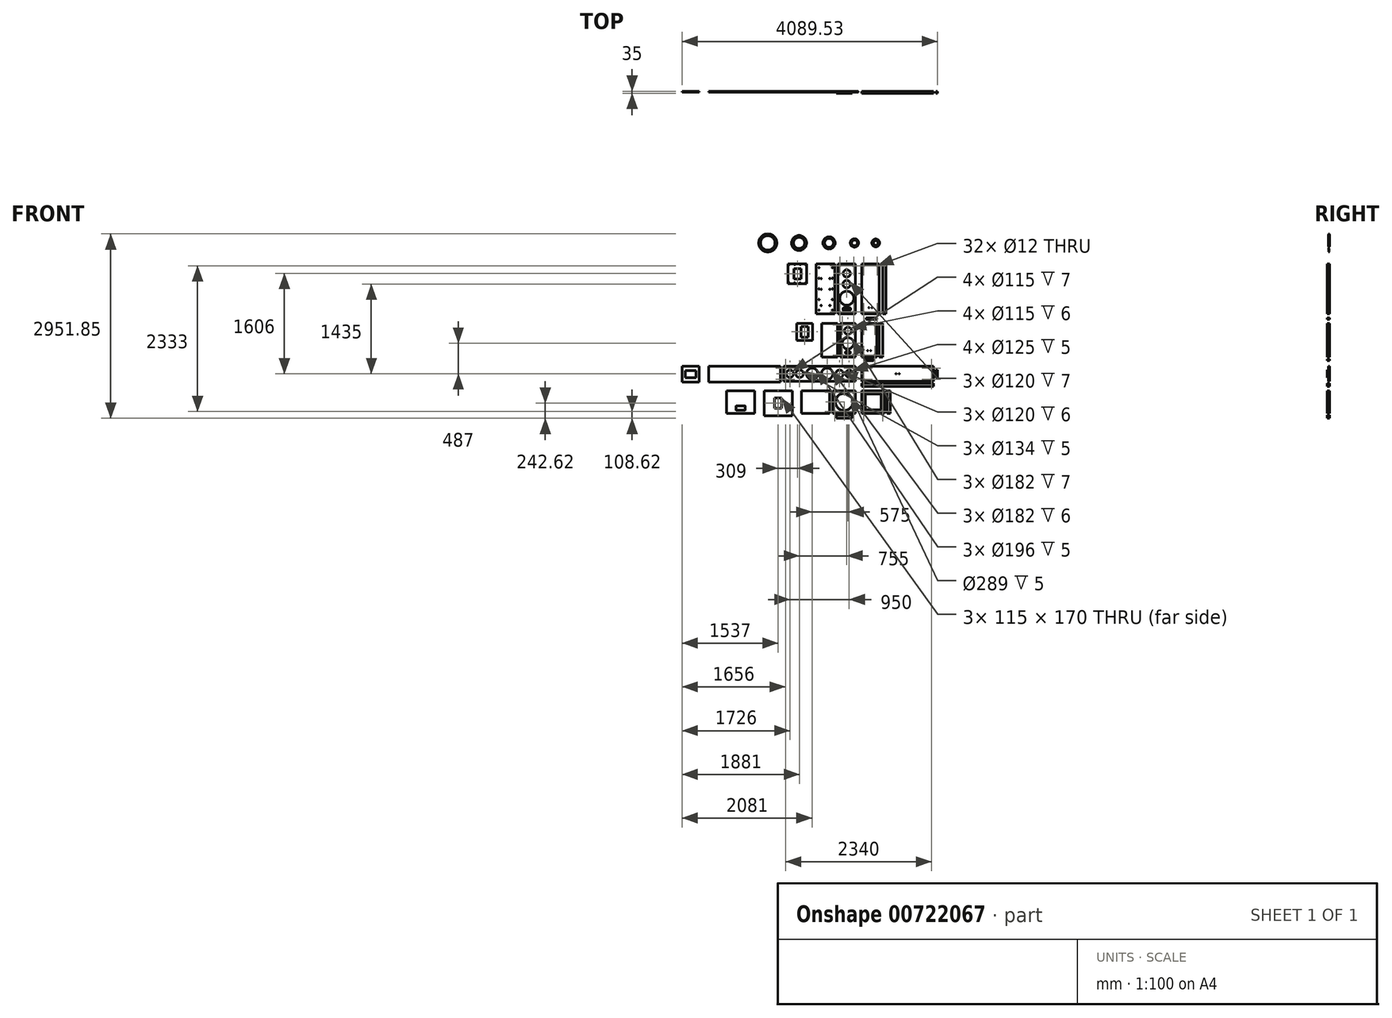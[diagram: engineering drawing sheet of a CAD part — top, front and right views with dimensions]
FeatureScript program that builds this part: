
annotation { "Feature Type Name" : "Feature", "Feature Type Description" : "" }
export const myFeature = defineFeature(function(context is Context, id is Id, definition is map)
    precondition{}
    {
        {
            assignVariable(context, id + "F0", {"name" : "WoodW", "anyValue" : 18});
        }
        {
            var Q0;
            Q0=qCreatedBy(makeId("Front.planeOp"),FACE);
            var sketch = newSketch(context, id + "F1", { "sketchPlane" : qUnion([Q0])});
            skLineSegment(sketch, "E0.bottom", {"start": v(0, 400) * mm, "end": v(-280, 400) * mm});
            skLineSegment(sketch, "E0.top", {"start": v(0, -400) * mm, "end": v(-280, -400) * mm});
            skLineSegment(sketch, "E0.left", {"start": v(0, 400) * mm, "end": v(0, -400) * mm});
            skLineSegment(sketch, "E0.right", {"start": v(-280, 400) * mm, "end": v(-280, -400) * mm});
            skLineSegment(sketch, "E1", {"start": v(-140, 400) * mm, "end": v(-140, -400) * mm, "construction": true});
            skCircle(sketch, "E2", {"center": v(-250, 370) * mm, "radius": 6 * mm});
            skCircle(sketch, "E3.MirrorC", {"center": v(-30, 370) * mm, "radius": 6 * mm});
            skCircle(sketch, "E4.MirrorC", {"center": v(-30, -370) * mm, "radius": 6 * mm});
            skCircle(sketch, "E5.MirrorC", {"center": v(-250, -370) * mm, "radius": 6 * mm});
            skLineSegment(sketch, "E6", {"start": v(50, -72.62) * mm, "end": v(50, -2297.12) * mm, "construction": true});
            skCircle(sketch, "E7.MirrorC", {"center": v(350, -370) * mm, "radius": 6 * mm});
            skCircle(sketch, "E8.MirrorC", {"center": v(130, -370) * mm, "radius": 6 * mm});
            skCircle(sketch, "E9.MirrorC", {"center": v(130, 370) * mm, "radius": 6 * mm});
            skCircle(sketch, "E10.MirrorC", {"center": v(350, 370) * mm, "radius": 6 * mm});
            skLineSegment(sketch, "E11.MirrorCS", {"start": v(100, 400) * mm, "end": v(380, 400) * mm});
            skLineSegment(sketch, "E12.MirrorCS", {"start": v(100, -400) * mm, "end": v(380, -400) * mm});
            skLineSegment(sketch, "E13.MirrorCS", {"start": v(100, 400) * mm, "end": v(100, -400) * mm});
            skLineSegment(sketch, "E14.MirrorCS", {"start": v(380, 400) * mm, "end": v(380, -400) * mm});
            skCircle(sketch, "E15", {"center": v(-140, -150) * mm, "radius": 112.5 * mm});
            skCircle(sketch, "E16", {"center": v(-140, 76) * mm, "radius": 60 * mm});
            skCircle(sketch, "E17", {"center": v(-140, 247) * mm, "radius": 57.5 * mm});
            skCircle(sketch, "E18.1.0", {"center": v(215, -300) * mm, "radius": 3.5 * mm});
            skLineSegment(sketch, "E19.bottom", {"start": v(-196, -305) * mm, "end": v(-84, -305) * mm});
            skLineSegment(sketch, "E19.top", {"start": v(-196, -345) * mm, "end": v(-84, -345) * mm});
            skLineSegment(sketch, "E19.left", {"start": v(-200, -309) * mm, "end": v(-200, -341) * mm});
            skLineSegment(sketch, "E19.right", {"start": v(-80, -309) * mm, "end": v(-80, -341) * mm});
            skPoint(sketch, "E20", {"position": v(-140, -305) * mm});
            skPoint(sketch, "E21.visualSharp", {"position": v(-200, -305) * mm});
            skArc(sketch, "E21.filletArc", {"start": v(-196, -305) * mm, "mid": v(-198.83, -306.17) * mm, "end": v(-200, -309) * mm});
            skPoint(sketch, "E22.visualSharp", {"position": v(-200, -345) * mm});
            skArc(sketch, "E22.filletArc", {"start": v(-200, -341) * mm, "mid": v(-198.83, -343.83) * mm, "end": v(-196, -345) * mm});
            skPoint(sketch, "E23.visualSharp", {"position": v(-80, -345) * mm});
            skArc(sketch, "E23.filletArc", {"start": v(-84, -345) * mm, "mid": v(-81.17, -343.83) * mm, "end": v(-80, -341) * mm});
            skPoint(sketch, "E24.visualSharp", {"position": v(-80, -305) * mm});
            skArc(sketch, "E24.filletArc", {"start": v(-80, -309) * mm, "mid": v(-81.17, -306.17) * mm, "end": v(-84, -305) * mm});
            skLineSegment(sketch, "E25.bottom", {"start": v(0, -550) * mm, "end": v(-240, -550) * mm});
            skLineSegment(sketch, "E25.top", {"start": v(0, -1089) * mm, "end": v(-240, -1089) * mm});
            skLineSegment(sketch, "E25.left", {"start": v(0, -550) * mm, "end": v(0, -1089) * mm});
            skLineSegment(sketch, "E25.right", {"start": v(-240, -550) * mm, "end": v(-240, -1089) * mm});
            skLineSegment(sketch, "E26", {"start": v(-120, -550) * mm, "end": v(-120, -1089) * mm, "construction": true});
            skCircle(sketch, "E27", {"center": v(-120, -671) * mm, "radius": 57.5 * mm});
            skCircle(sketch, "E28", {"center": v(-120, -872) * mm, "radius": 91 * mm});
            skCircle(sketch, "E29", {"center": v(-210, -580) * mm, "radius": 6 * mm});
            skLineSegment(sketch, "E30", {"start": v(-240, -819.5) * mm, "end": v(0, -819.5) * mm, "construction": true});
            skCircle(sketch, "E31.MirrorC", {"center": v(-210, -1059) * mm, "radius": 6 * mm});
            skCircle(sketch, "E32.MirrorC", {"center": v(-30, -1059) * mm, "radius": 6 * mm});
            skCircle(sketch, "E33.MirrorC", {"center": v(-30, -580) * mm, "radius": 6 * mm});
            skLineSegment(sketch, "E34.MirrorCS", {"start": v(100, -550) * mm, "end": v(100, -1089) * mm});
            skLineSegment(sketch, "E35.MirrorCS", {"start": v(100, -550) * mm, "end": v(340, -550) * mm});
            skLineSegment(sketch, "E36.MirrorCS", {"start": v(340, -550) * mm, "end": v(340, -1089) * mm});
            skLineSegment(sketch, "E37.MirrorCS", {"start": v(100, -1089) * mm, "end": v(340, -1089) * mm});
            skCircle(sketch, "E38.MirrorC", {"center": v(130, -1059) * mm, "radius": 6 * mm});
            skCircle(sketch, "E39.MirrorC", {"center": v(310, -1059) * mm, "radius": 6 * mm});
            skCircle(sketch, "E40.MirrorC", {"center": v(130, -580) * mm, "radius": 6 * mm});
            skCircle(sketch, "E41.MirrorC", {"center": v(310, -580) * mm, "radius": 6 * mm});
            skLineSegment(sketch, "E42.bottom", {"start": v(-153.5, -1004) * mm, "end": v(-86.5, -1004) * mm});
            skLineSegment(sketch, "E42.top", {"start": v(-153.5, -1034) * mm, "end": v(-86.5, -1034) * mm});
            skLineSegment(sketch, "E42.left", {"start": v(-157.5, -1008) * mm, "end": v(-157.5, -1030) * mm});
            skLineSegment(sketch, "E42.right", {"start": v(-82.5, -1008) * mm, "end": v(-82.5, -1030) * mm});
            skPoint(sketch, "E43", {"position": v(-120, -1004) * mm});
            skLineSegment(sketch, "E44", {"start": v(220, -550) * mm, "end": v(220, -1089) * mm, "construction": true});
            skPoint(sketch, "E45.visualSharp", {"position": v(-157.5, -1004) * mm});
            skArc(sketch, "E45.filletArc", {"start": v(-153.5, -1004) * mm, "mid": v(-156.33, -1005.17) * mm, "end": v(-157.5, -1008) * mm});
            skPoint(sketch, "E46.visualSharp", {"position": v(-157.5, -1034) * mm});
            skArc(sketch, "E46.filletArc", {"start": v(-157.5, -1030) * mm, "mid": v(-156.33, -1032.83) * mm, "end": v(-153.5, -1034) * mm});
            skPoint(sketch, "E47.visualSharp", {"position": v(-82.5, -1034) * mm});
            skArc(sketch, "E47.filletArc", {"start": v(-86.5, -1034) * mm, "mid": v(-83.67, -1032.83) * mm, "end": v(-82.5, -1030) * mm});
            skPoint(sketch, "E48.visualSharp", {"position": v(-82.5, -1004) * mm});
            skArc(sketch, "E48.filletArc", {"start": v(-82.5, -1008) * mm, "mid": v(-83.67, -1005.17) * mm, "end": v(-86.5, -1004) * mm});
            skLineSegment(sketch, "E49.bottom", {"start": v(0, -1239) * mm, "end": v(-1150, -1239) * mm});
            skLineSegment(sketch, "E49.top", {"start": v(0, -1479) * mm, "end": v(-1150, -1479) * mm});
            skLineSegment(sketch, "E49.left", {"start": v(0, -1239) * mm, "end": v(0, -1479) * mm});
            skLineSegment(sketch, "E49.right", {"start": v(-1150, -1239) * mm, "end": v(-1150, -1479) * mm});
            skLineSegment(sketch, "E50", {"start": v(-1150, -1359) * mm, "end": v(0, -1359) * mm, "construction": true});
            skLineSegment(sketch, "E51", {"start": v(-575, -1239) * mm, "end": v(-575, -1479) * mm, "construction": true});
            skCircle(sketch, "E52", {"center": v(-1120, -1269) * mm, "radius": 6 * mm});
            skCircle(sketch, "E53.MirrorC", {"center": v(-1120, -1449) * mm, "radius": 6 * mm});
            skCircle(sketch, "E54.MirrorC", {"center": v(-30, -1449) * mm, "radius": 6 * mm});
            skCircle(sketch, "E55.MirrorC", {"center": v(-30, -1269) * mm, "radius": 6 * mm});
            skCircle(sketch, "E56.MirrorC", {"center": v(130, -1269) * mm, "radius": 6 * mm});
            skCircle(sketch, "E57.MirrorC", {"center": v(130, -1449) * mm, "radius": 6 * mm});
            skCircle(sketch, "E58.MirrorC", {"center": v(1220, -1269) * mm, "radius": 6 * mm});
            skLineSegment(sketch, "E59.MirrorCS", {"start": v(1250, -1359) * mm, "end": v(100, -1359) * mm, "construction": true});
            skCircle(sketch, "E60.MirrorC", {"center": v(1220, -1449) * mm, "radius": 6 * mm});
            skLineSegment(sketch, "E61.MirrorCS", {"start": v(1250, -1239) * mm, "end": v(1250, -1479) * mm});
            skLineSegment(sketch, "E62.MirrorCS", {"start": v(675, -1239) * mm, "end": v(675, -1479) * mm, "construction": true});
            skLineSegment(sketch, "E63.MirrorCS", {"start": v(100, -1239) * mm, "end": v(100, -1479) * mm});
            skLineSegment(sketch, "E64.MirrorCS", {"start": v(100, -1239) * mm, "end": v(1250, -1239) * mm});
            skLineSegment(sketch, "E65.MirrorCS", {"start": v(100, -1479) * mm, "end": v(1250, -1479) * mm});
            skCircle(sketch, "E66", {"center": v(-100, -1359) * mm, "radius": 57.5 * mm});
            skCircle(sketch, "E67", {"center": v(-255, -1359) * mm, "radius": 60 * mm});
            skCircle(sketch, "E68", {"center": v(-455, -1359) * mm, "radius": 91 * mm});
            skCircle(sketch, "E69.MirrorC", {"center": v(-895, -1359) * mm, "radius": 60 * mm});
            skCircle(sketch, "E70.MirrorC", {"center": v(-1050, -1359) * mm, "radius": 57.5 * mm});
            skCircle(sketch, "E71.MirrorC", {"center": v(-695, -1359) * mm, "radius": 91 * mm});
            skLineSegment(sketch, "E72.bottom", {"start": v(0, -1629) * mm, "end": v(-364, -1629) * mm});
            skLineSegment(sketch, "E72.top", {"start": v(0, -1993) * mm, "end": v(-364, -1993) * mm});
            skLineSegment(sketch, "E72.left", {"start": v(0, -1629) * mm, "end": v(0, -1993) * mm});
            skLineSegment(sketch, "E72.right", {"start": v(-364, -1629) * mm, "end": v(-364, -1993) * mm});
            skLineSegment(sketch, "E73", {"start": v(-182, -1629) * mm, "end": v(-182, -1993) * mm, "construction": true});
            skLineSegment(sketch, "E74", {"start": v(-364, -1811) * mm, "end": v(0, -1811) * mm, "construction": true});
            skCircle(sketch, "E75", {"center": v(-334, -1659) * mm, "radius": 6 * mm});
            skCircle(sketch, "E76.MirrorC", {"center": v(-30, -1659) * mm, "radius": 6 * mm});
            skCircle(sketch, "E77.MirrorC", {"center": v(-334, -1963) * mm, "radius": 6 * mm});
            skCircle(sketch, "E78.MirrorC", {"center": v(-30, -1963) * mm, "radius": 6 * mm});
            skCircle(sketch, "E79.MirrorC", {"center": v(130, -1963) * mm, "radius": 6 * mm});
            skCircle(sketch, "E80.MirrorC", {"center": v(434, -1963) * mm, "radius": 6 * mm});
            skCircle(sketch, "E81.MirrorC", {"center": v(434, -1659) * mm, "radius": 6 * mm});
            skCircle(sketch, "E82.MirrorC", {"center": v(130, -1659) * mm, "radius": 6 * mm});
            skLineSegment(sketch, "E83.MirrorCS", {"start": v(464, -1629) * mm, "end": v(464, -1993) * mm});
            skLineSegment(sketch, "E84.MirrorCS", {"start": v(100, -1629) * mm, "end": v(100, -1993) * mm});
            skLineSegment(sketch, "E85.MirrorCS", {"start": v(100, -1993) * mm, "end": v(464, -1993) * mm});
            skLineSegment(sketch, "E86.MirrorCS", {"start": v(282, -1629) * mm, "end": v(282, -1993) * mm, "construction": true});
            skLineSegment(sketch, "E87.MirrorCS", {"start": v(100, -1629) * mm, "end": v(464, -1629) * mm});
            skLineSegment(sketch, "E88.MirrorCS", {"start": v(464, -1811) * mm, "end": v(100, -1811) * mm, "construction": true});
            skCircle(sketch, "E89", {"center": v(-182, -1811) * mm, "radius": 137.5 * mm});
            skLineSegment(sketch, "E90.bottom", {"start": v(158.5, -1683.5) * mm, "end": v(405.5, -1683.5) * mm});
            skLineSegment(sketch, "E90.top", {"start": v(158.5, -1938.5) * mm, "end": v(405.5, -1938.5) * mm});
            skLineSegment(sketch, "E90.left", {"start": v(154.5, -1687.5) * mm, "end": v(154.5, -1934.5) * mm});
            skLineSegment(sketch, "E90.right", {"start": v(409.5, -1687.5) * mm, "end": v(409.5, -1934.5) * mm});
            skPoint(sketch, "E91", {"position": v(282, -1683.5) * mm});
            skLineSegment(sketch, "E92", {"start": v(154.5, -1811) * mm, "end": v(409.5, -1811) * mm, "construction": true});
            skPoint(sketch, "E93.visualSharp", {"position": v(154.5, -1683.5) * mm});
            skArc(sketch, "E93.filletArc", {"start": v(158.5, -1683.5) * mm, "mid": v(155.67, -1684.67) * mm, "end": v(154.5, -1687.5) * mm});
            skPoint(sketch, "E94.visualSharp", {"position": v(154.5, -1938.5) * mm});
            skArc(sketch, "E94.filletArc", {"start": v(154.5, -1934.5) * mm, "mid": v(155.67, -1937.33) * mm, "end": v(158.5, -1938.5) * mm});
            skPoint(sketch, "E95.visualSharp", {"position": v(409.5, -1938.5) * mm});
            skArc(sketch, "E95.filletArc", {"start": v(405.5, -1938.5) * mm, "mid": v(408.33, -1937.33) * mm, "end": v(409.5, -1934.5) * mm});
            skPoint(sketch, "E96.visualSharp", {"position": v(409.5, -1683.5) * mm});
            skArc(sketch, "E96.filletArc", {"start": v(409.5, -1687.5) * mm, "mid": v(408.33, -1684.67) * mm, "end": v(405.5, -1683.5) * mm});
            skLineSegment(sketch, "E97", {"start": v(240, -400) * mm, "end": v(240, 400) * mm, "construction": true});
            skCircle(sketch, "E98.MirrorC", {"center": v(265, -300) * mm, "radius": 3.5 * mm});
            skCircle(sketch, "E99", {"center": v(195, -989) * mm, "radius": 3.5 * mm});
            skCircle(sketch, "E100.MirrorC", {"center": v(245, -989) * mm, "radius": 3.5 * mm});
            skCircle(sketch, "E101", {"center": v(650, -1359) * mm, "radius": 3.5 * mm});
            skCircle(sketch, "E102.MirrorC", {"center": v(700, -1359) * mm, "radius": 3.5 * mm});
            skSolve(sketch);
        }
        {
            var Q0;
            Q0=qSketchRegion(id+"F1",true);
            extrude(context, id + "F2", {"entities" : qUnion([Q0]), "depth" : 18 * mm, "offsetDistance" : 25 * mm});
        }
        {
            var Q0;
            Q0=qCreatedBy(makeId("Front.planeOp"),FACE);
            var sketch = newSketch(context, id + "F3", { "sketchPlane" : qUnion([Q0])});
            skLineSegment(sketch, "E103.bottom", {"start": v(-330, 400) * mm, "end": v(-630, 400) * mm});
            skLineSegment(sketch, "E103.top", {"start": v(-330, -400) * mm, "end": v(-630, -400) * mm});
            skLineSegment(sketch, "E103.left", {"start": v(-330, 400) * mm, "end": v(-330, -400) * mm});
            skLineSegment(sketch, "E103.right", {"start": v(-630, 400) * mm, "end": v(-630, -400) * mm});
            skLineSegment(sketch, "E104.bottom", {"start": v(-780, 400) * mm, "end": v(-1080, 400) * mm});
            skLineSegment(sketch, "E104.top", {"start": v(-780, 84) * mm, "end": v(-1080, 84) * mm});
            skLineSegment(sketch, "E104.left", {"start": v(-780, 400) * mm, "end": v(-780, 84) * mm});
            skLineSegment(sketch, "E104.right", {"start": v(-1080, 400) * mm, "end": v(-1080, 84) * mm});
            skLineSegment(sketch, "E105.bottom", {"start": v(-290, -550) * mm, "end": v(-540, -550) * mm});
            skLineSegment(sketch, "E105.top", {"start": v(-290, -1089) * mm, "end": v(-540, -1089) * mm});
            skLineSegment(sketch, "E105.left", {"start": v(-290, -550) * mm, "end": v(-290, -1089) * mm});
            skLineSegment(sketch, "E105.right", {"start": v(-540, -550) * mm, "end": v(-540, -1089) * mm});
            skLineSegment(sketch, "E106.bottom", {"start": v(-690, -550) * mm, "end": v(-940, -550) * mm});
            skLineSegment(sketch, "E106.top", {"start": v(-690, -826) * mm, "end": v(-940, -826) * mm});
            skLineSegment(sketch, "E106.left", {"start": v(-690, -550) * mm, "end": v(-690, -826) * mm});
            skLineSegment(sketch, "E106.right", {"start": v(-940, -550) * mm, "end": v(-940, -826) * mm});
            skLineSegment(sketch, "E107.bottom", {"start": v(-1200, -1239) * mm, "end": v(-2350, -1239) * mm});
            skLineSegment(sketch, "E107.top", {"start": v(-1200, -1489) * mm, "end": v(-2350, -1489) * mm});
            skLineSegment(sketch, "E107.left", {"start": v(-1200, -1239) * mm, "end": v(-1200, -1489) * mm});
            skLineSegment(sketch, "E107.right", {"start": v(-2350, -1239) * mm, "end": v(-2350, -1489) * mm});
            skLineSegment(sketch, "E108.bottom", {"start": v(-2500, -1239) * mm, "end": v(-2776, -1239) * mm});
            skLineSegment(sketch, "E108.top", {"start": v(-2500, -1489) * mm, "end": v(-2776, -1489) * mm});
            skLineSegment(sketch, "E108.left", {"start": v(-2500, -1239) * mm, "end": v(-2500, -1489) * mm});
            skLineSegment(sketch, "E108.right", {"start": v(-2776, -1239) * mm, "end": v(-2776, -1489) * mm});
            skLineSegment(sketch, "E109.bottom", {"start": v(-414, -1629) * mm, "end": v(-864, -1629) * mm});
            skLineSegment(sketch, "E109.top", {"start": v(-414, -1993) * mm, "end": v(-864, -1993) * mm});
            skLineSegment(sketch, "E109.left", {"start": v(-414, -1629) * mm, "end": v(-414, -1993) * mm});
            skLineSegment(sketch, "E109.right", {"start": v(-864, -1629) * mm, "end": v(-864, -1993) * mm});
            skLineSegment(sketch, "E110.bottom", {"start": v(-1014, -1629) * mm, "end": v(-1464, -1629) * mm});
            skLineSegment(sketch, "E110.top", {"start": v(-1014, -2029) * mm, "end": v(-1464, -2029) * mm});
            skLineSegment(sketch, "E110.left", {"start": v(-1014, -1629) * mm, "end": v(-1014, -2029) * mm});
            skLineSegment(sketch, "E110.right", {"start": v(-1464, -1629) * mm, "end": v(-1464, -2029) * mm});
            skLineSegment(sketch, "E111.bottom", {"start": v(-987.5, 327) * mm, "end": v(-872.5, 327) * mm});
            skLineSegment(sketch, "E111.top", {"start": v(-987.5, 157) * mm, "end": v(-872.5, 157) * mm});
            skLineSegment(sketch, "E111.left", {"start": v(-987.5, 327) * mm, "end": v(-987.5, 157) * mm});
            skLineSegment(sketch, "E111.right", {"start": v(-872.5, 327) * mm, "end": v(-872.5, 157) * mm});
            skLineSegment(sketch, "E112", {"start": v(-930, 400) * mm, "end": v(-930, 84) * mm, "construction": true});
            skLineSegment(sketch, "E113", {"start": v(-1080, 242) * mm, "end": v(-780, 242) * mm, "construction": true});
            skPoint(sketch, "E114", {"position": v(-930, 327) * mm});
            skPoint(sketch, "E115", {"position": v(-987.5, 242) * mm});
            skLineSegment(sketch, "E116", {"start": v(-815, -550) * mm, "end": v(-815, -826) * mm, "construction": true});
            skLineSegment(sketch, "E117", {"start": v(-940, -688) * mm, "end": v(-690, -688) * mm, "construction": true});
            skLineSegment(sketch, "E118.bottom", {"start": v(-872.5, -603) * mm, "end": v(-757.5, -603) * mm});
            skLineSegment(sketch, "E118.top", {"start": v(-872.5, -773) * mm, "end": v(-757.5, -773) * mm});
            skLineSegment(sketch, "E118.left", {"start": v(-872.5, -603) * mm, "end": v(-872.5, -773) * mm});
            skLineSegment(sketch, "E118.right", {"start": v(-757.5, -603) * mm, "end": v(-757.5, -773) * mm});
            skPoint(sketch, "E119", {"position": v(-815, -603) * mm});
            skPoint(sketch, "E120", {"position": v(-757.5, -688) * mm});
            skLineSegment(sketch, "E121", {"start": v(-2638, -1239) * mm, "end": v(-2638, -1489) * mm, "construction": true});
            skLineSegment(sketch, "E122", {"start": v(-2500, -1364) * mm, "end": v(-2776, -1364) * mm, "construction": true});
            skLineSegment(sketch, "E123.bottom", {"start": v(-2553, -1421.5) * mm, "end": v(-2723, -1421.5) * mm});
            skLineSegment(sketch, "E123.top", {"start": v(-2553, -1306.5) * mm, "end": v(-2723, -1306.5) * mm});
            skLineSegment(sketch, "E123.left", {"start": v(-2553, -1421.5) * mm, "end": v(-2553, -1306.5) * mm});
            skLineSegment(sketch, "E123.right", {"start": v(-2723, -1421.5) * mm, "end": v(-2723, -1306.5) * mm});
            skPoint(sketch, "E124", {"position": v(-2638, -1306.5) * mm});
            skPoint(sketch, "E125", {"position": v(-2553, -1364) * mm});
            skLineSegment(sketch, "E126", {"start": v(-1239, -1629) * mm, "end": v(-1239, -2029) * mm, "construction": true});
            skLineSegment(sketch, "E127", {"start": v(-1014, -1829) * mm, "end": v(-1464, -1829) * mm, "construction": true});
            skLineSegment(sketch, "E128.bottom", {"start": v(-1181.5, -1914) * mm, "end": v(-1296.5, -1914) * mm});
            skLineSegment(sketch, "E128.top", {"start": v(-1181.5, -1744) * mm, "end": v(-1296.5, -1744) * mm});
            skLineSegment(sketch, "E128.left", {"start": v(-1181.5, -1914) * mm, "end": v(-1181.5, -1744) * mm});
            skLineSegment(sketch, "E128.right", {"start": v(-1296.5, -1914) * mm, "end": v(-1296.5, -1744) * mm});
            skPoint(sketch, "E129", {"position": v(-1239, -1744) * mm});
            skPoint(sketch, "E130", {"position": v(-1181.5, -1829) * mm});
            skLineSegment(sketch, "E131.bottom", {"start": v(-1614, -1629) * mm, "end": v(-2064, -1629) * mm});
            skLineSegment(sketch, "E131.top", {"start": v(-1614, -1993) * mm, "end": v(-2064, -1993) * mm});
            skLineSegment(sketch, "E131.left", {"start": v(-1614, -1629) * mm, "end": v(-1614, -1993) * mm});
            skLineSegment(sketch, "E131.right", {"start": v(-2064, -1629) * mm, "end": v(-2064, -1993) * mm});
            skLineSegment(sketch, "E132.bottom", {"start": v(-1910, -1873) * mm, "end": v(-1768, -1873) * mm});
            skLineSegment(sketch, "E132.top", {"start": v(-1910, -1943) * mm, "end": v(-1768, -1943) * mm});
            skLineSegment(sketch, "E132.left", {"start": v(-1914, -1877) * mm, "end": v(-1914, -1939) * mm});
            skLineSegment(sketch, "E132.right", {"start": v(-1764, -1877) * mm, "end": v(-1764, -1939) * mm});
            skLineSegment(sketch, "E133", {"start": v(-1839, -1629) * mm, "end": v(-1839, -1993) * mm, "construction": true});
            skPoint(sketch, "E134", {"position": v(-1839, -1873) * mm});
            skPoint(sketch, "E135.visualSharp", {"position": v(-1764, -1873) * mm});
            skArc(sketch, "E135.filletArc", {"start": v(-1764, -1877) * mm, "mid": v(-1765.17, -1874.17) * mm, "end": v(-1768, -1873) * mm});
            skPoint(sketch, "E136.visualSharp", {"position": v(-1764, -1943) * mm});
            skArc(sketch, "E136.filletArc", {"start": v(-1768, -1943) * mm, "mid": v(-1765.17, -1941.83) * mm, "end": v(-1764, -1939) * mm});
            skPoint(sketch, "E137.visualSharp", {"position": v(-1914, -1943) * mm});
            skArc(sketch, "E137.filletArc", {"start": v(-1914, -1939) * mm, "mid": v(-1912.83, -1941.83) * mm, "end": v(-1910, -1943) * mm});
            skPoint(sketch, "E138.visualSharp", {"position": v(-1914, -1873) * mm});
            skArc(sketch, "E138.filletArc", {"start": v(-1910, -1873) * mm, "mid": v(-1912.83, -1874.17) * mm, "end": v(-1914, -1877) * mm});
            skSolve(sketch);
        }
        {
            var Q0;
            Q0=qSketchRegion(id+"F3",true);
            extrude(context, id + "F4", {"entities" : qUnion([Q0]), "depth" : (getVariable(context, 'WoodW')) * mm, "offsetDistance" : 25 * mm});
        }
        {
            var Q0;
            Q0=qCreatedBy(makeId("Front.planeOp"),FACE);
            var sketch = newSketch(context, id + "F5", { "sketchPlane" : qUnion([Q0])});
            skCircle(sketch, "E139", {"center": v(-1404.17, 735.73) * mm, "radius": 137.5 * mm});
            skCircle(sketch, "E140", {"center": v(-903.37, 735.73) * mm, "radius": 112.5 * mm});
            skCircle(sketch, "E141", {"center": v(-423.44, 735.73) * mm, "radius": 91 * mm});
            skCircle(sketch, "E142", {"center": v(-16.54, 735.73) * mm, "radius": 46 * mm});
            skCircle(sketch, "E143", {"center": v(324.28, 735.73) * mm, "radius": 57.5 * mm});
            skCircle(sketch, "E144", {"center": v(-1404.17, 735.73) * mm, "radius": 116 * mm});
            skCircle(sketch, "E145", {"center": v(-903.37, 735.73) * mm, "radius": 89 * mm});
            skCircle(sketch, "E146", {"center": v(-423.44, 735.73) * mm, "radius": 71 * mm});
            skCircle(sketch, "E147", {"center": v(-16.54, 735.73) * mm, "radius": 60 * mm});
            skCircle(sketch, "E148", {"center": v(324.28, 735.73) * mm, "radius": 37 * mm});
            skSolve(sketch);
        }
        {
            var Q0;
            Q0=qSketchRegion(id+"F5",true);
            extrude(context, id + "F6", {"entities" : qUnion([Q0]), "depth" : 18 * mm, "offsetDistance" : 25 * mm});
        }
        {
            var Q0;
            Q0=qCreatedBy(makeId("Front.planeOp"),FACE);
            cPlane(context, id + "F7", {"entities" : qUnion([Q0]), "cplaneType" : CPlaneType.OFFSET, "offset" : 7 * mm, "width" : 150 * mm, "height" : 150 * mm});
        }
        {
            var Q0;
            Q0=qCreatedBy(id+"F7.planeOp",FACE);
            var sketch = newSketch(context, id + "F8", { "sketchPlane" : qUnion([Q0])});
            skCircle(sketch, "E149", {"center": v(324.28, 735.73) * mm, "radius": 62.5 * mm});
            skCircle(sketch, "E150", {"center": v(324.28, 735.73) * mm, "radius": 37 * mm});
            skCircle(sketch, "E151", {"center": v(-16.54, 735.73) * mm, "radius": 46 * mm});
            skCircle(sketch, "E152", {"center": v(-16.54, 735.73) * mm, "radius": 67 * mm});
            skCircle(sketch, "E153", {"center": v(-423.44, 735.73) * mm, "radius": 71 * mm});
            skCircle(sketch, "E154", {"center": v(-423.44, 735.73) * mm, "radius": 98 * mm});
            skCircle(sketch, "E155", {"center": v(-903.37, 735.73) * mm, "radius": 89 * mm});
            skCircle(sketch, "E156", {"center": v(-903.37, 735.73) * mm, "radius": 119.5 * mm});
            skCircle(sketch, "E157", {"center": v(-1404.17, 735.73) * mm, "radius": 116 * mm});
            skCircle(sketch, "E158", {"center": v(-1404.17, 735.73) * mm, "radius": 144.5 * mm});
            skSolve(sketch);
        }
        {
            var Q0;
            Q0=qSketchRegion(id+"F8",true);
            extrude(context, id + "F9", {"entities" : qUnion([Q0]), "operationType" : NewBodyOperationType.ADD, "depth" : 4 * mm, "offsetDistance" : 25 * mm});
        }
        {
            var Q0;
            Q0=makeQuery(id+"F6.opExtrude","CAP_EDGE",EDGE,{"disambiguationData":[OSD([sQuery(id+"F5.wireOp",EDGE,"E144")])],"isStart":false});
            var Q1;
            Q1=makeQuery(id+"F6.opExtrude","CAP_EDGE",EDGE,{"disambiguationData":[OSD([sQuery(id+"F5.wireOp",EDGE,"E145")])],"isStart":false});
            var Q2;
            Q2=makeQuery(id+"F6.opExtrude","CAP_EDGE",EDGE,{"disambiguationData":[OSD([sQuery(id+"F5.wireOp",EDGE,"E146")])],"isStart":false});
            var Q3;
            Q3=makeQuery(id+"F6.opExtrude","CAP_EDGE",EDGE,{"disambiguationData":[OSD([sQuery(id+"F5.wireOp",EDGE,"E142")])],"isStart":false});
            var Q4;
            Q4=makeQuery(id+"F6.opExtrude","CAP_EDGE",EDGE,{"disambiguationData":[OSD([sQuery(id+"F5.wireOp",EDGE,"E148")])],"isStart":false});
            chamfer(context, id + "F10", {"entities" : qUnion([Q0, Q1, Q2, Q3, Q4]), "width" : 8 * mm, "tangentPropagation" : true});
        }
        {
            var Q0;
            Q0=qCreatedBy(id+"F7.planeOp",FACE);
            var sketch = newSketch(context, id + "F11", { "sketchPlane" : qUnion([Q0])});
            skCircle(sketch, "E159", {"center": v(-140, 247) * mm, "radius": 62.5 * mm});
            skCircle(sketch, "E160", {"center": v(-140, 76) * mm, "radius": 67 * mm});
            skCircle(sketch, "E161", {"center": v(-140, -150) * mm, "radius": 119.5 * mm});
            skCircle(sketch, "E162", {"center": v(-120, -671) * mm, "radius": 62.5 * mm});
            skCircle(sketch, "E163", {"center": v(-120, -872) * mm, "radius": 98 * mm});
            skCircle(sketch, "E164", {"center": v(-1050, -1359) * mm, "radius": 62.5 * mm});
            skCircle(sketch, "E165", {"center": v(-895, -1359) * mm, "radius": 67 * mm});
            skCircle(sketch, "E166", {"center": v(-695, -1359) * mm, "radius": 98 * mm});
            skCircle(sketch, "E167", {"center": v(-182, -1811) * mm, "radius": 144.5 * mm});
            skLineSegment(sketch, "E168", {"start": v(-575, -1239) * mm, "end": v(-575, -1479) * mm, "construction": true});
            skCircle(sketch, "E169.MirrorC", {"center": v(-455, -1359) * mm, "radius": 98 * mm});
            skCircle(sketch, "E170.MirrorC", {"center": v(-255, -1359) * mm, "radius": 67 * mm});
            skCircle(sketch, "E171.MirrorC", {"center": v(-100, -1359) * mm, "radius": 62.5 * mm});
            skSolve(sketch);
        }
        {
            var Q0;
            Q0=qSketchRegion(id+"F11",true);
            extrude(context, id + "F12", {"entities" : qUnion([Q0]), "operationType" : NewBodyOperationType.REMOVE, "depth" : 5 * mm, "offsetDistance" : 25 * mm});
        }
        {
            var Q0;
            Q0=qCreatedBy(makeId("Front.planeOp"),FACE);
            var sketch = newSketch(context, id + "F13", { "sketchPlane" : qUnion([Q0])});
            skLineSegment(sketch, "E172.bottom", {"start": v(434.57, 400) * mm, "end": v(489.57, 400) * mm});
            skLineSegment(sketch, "E172.top", {"start": v(434.57, -400) * mm, "end": v(489.57, -400) * mm});
            skLineSegment(sketch, "E172.left", {"start": v(434.57, 400) * mm, "end": v(434.57, -400) * mm});
            skLineSegment(sketch, "E172.right", {"start": v(489.57, 400) * mm, "end": v(489.57, -400) * mm});
            skLineSegment(sketch, "E173.bottom", {"start": v(381.48, -550) * mm, "end": v(436.48, -550) * mm});
            skLineSegment(sketch, "E173.top", {"start": v(381.48, -1089) * mm, "end": v(436.48, -1089) * mm});
            skLineSegment(sketch, "E173.left", {"start": v(381.48, -550) * mm, "end": v(381.48, -1089) * mm});
            skLineSegment(sketch, "E173.right", {"start": v(436.48, -550) * mm, "end": v(436.48, -1089) * mm});
            skLineSegment(sketch, "E174.bottom", {"start": v(505.02, -1629) * mm, "end": v(560.02, -1629) * mm});
            skLineSegment(sketch, "E174.top", {"start": v(505.02, -1993) * mm, "end": v(560.02, -1993) * mm});
            skLineSegment(sketch, "E174.left", {"start": v(505.02, -1629) * mm, "end": v(505.02, -1993) * mm});
            skLineSegment(sketch, "E174.right", {"start": v(560.02, -1629) * mm, "end": v(560.02, -1993) * mm});
            skLineSegment(sketch, "E175.bottom", {"start": v(100, -1508.51) * mm, "end": v(1250, -1508.51) * mm});
            skLineSegment(sketch, "E175.top", {"start": v(100, -1563.51) * mm, "end": v(1250, -1563.51) * mm});
            skLineSegment(sketch, "E175.left", {"start": v(100, -1508.51) * mm, "end": v(100, -1563.51) * mm});
            skLineSegment(sketch, "E175.right", {"start": v(1250, -1508.51) * mm, "end": v(1250, -1563.51) * mm});
            skLineSegment(sketch, "E176.bottom", {"start": v(1286.03, -1293.88) * mm, "end": v(1313.53, -1293.88) * mm});
            skLineSegment(sketch, "E176.top", {"start": v(1286.03, -1423.88) * mm, "end": v(1313.53, -1423.88) * mm});
            skLineSegment(sketch, "E176.left", {"start": v(1286.03, -1293.88) * mm, "end": v(1286.03, -1423.88) * mm});
            skLineSegment(sketch, "E176.right", {"start": v(1313.53, -1293.88) * mm, "end": v(1313.53, -1423.88) * mm});
            skLineSegment(sketch, "E177.bottom", {"start": v(157.38, -1122.26) * mm, "end": v(287.38, -1122.26) * mm});
            skLineSegment(sketch, "E177.top", {"start": v(157.38, -1149.76) * mm, "end": v(287.38, -1149.76) * mm});
            skLineSegment(sketch, "E177.left", {"start": v(157.38, -1122.26) * mm, "end": v(157.38, -1149.76) * mm});
            skLineSegment(sketch, "E177.right", {"start": v(287.38, -1122.26) * mm, "end": v(287.38, -1149.76) * mm});
            skLineSegment(sketch, "E178.bottom", {"start": v(171.4, -461.79) * mm, "end": v(341.4, -461.79) * mm});
            skLineSegment(sketch, "E178.top", {"start": v(171.4, -489.29) * mm, "end": v(341.4, -489.29) * mm});
            skLineSegment(sketch, "E178.left", {"start": v(171.4, -461.79) * mm, "end": v(171.4, -489.29) * mm});
            skLineSegment(sketch, "E178.right", {"start": v(341.4, -461.79) * mm, "end": v(341.4, -489.29) * mm});
            skLineSegment(sketch, "E179.bottom", {"start": v(-306.03, -2016.62) * mm, "end": v(-52.03, -2016.62) * mm});
            skLineSegment(sketch, "E179.top", {"start": v(-306.03, -2071.62) * mm, "end": v(-52.03, -2071.62) * mm});
            skLineSegment(sketch, "E179.left", {"start": v(-306.03, -2016.62) * mm, "end": v(-306.03, -2071.62) * mm});
            skLineSegment(sketch, "E179.right", {"start": v(-52.03, -2016.62) * mm, "end": v(-52.03, -2071.62) * mm});
            skSolve(sketch);
        }
        {
            var Q0;
            Q0 = qSketchRegion(id + "F13", true);
            extrude(context, id + "F14", {"entities" : qUnion([Q0]), "depth" : 35 * mm, "offsetDistance" : 25 * mm});
        }
        {
            var Q0;
            Q0=makeQuery(id+"F4.opExtrude","CAP_FACE",FACE,{"disambiguationData":[OSD([sQuery(id+"F3.wireOp",EDGE,"E103.bottom"),sQuery(id+"F3.wireOp",EDGE,"E103.top"),sQuery(id+"F3.wireOp",EDGE,"E103.left"),sQuery(id+"F3.wireOp",EDGE,"E103.right")])],"isStart":false});
            var sketch = newSketch(context, id + "F15", { "sketchPlane" : qUnion([Q0])});
            skPoint(sketch, "E180", {"position": v(-585, -340) * mm});
            skPoint(sketch, "E181", {"position": v(-370, -340) * mm});
            skPoint(sketch, "E182", {"position": v(-370, -170) * mm});
            skPoint(sketch, "E183", {"position": v(-370, 0) * mm});
            skPoint(sketch, "E184", {"position": v(-370, 170) * mm});
            skPoint(sketch, "E185", {"position": v(-370, 340) * mm});
            skPoint(sketch, "E186", {"position": v(-585, 340) * mm});
            skPoint(sketch, "E187", {"position": v(-585, 170) * mm});
            skPoint(sketch, "E188", {"position": v(-585, 0) * mm});
            skPoint(sketch, "E189", {"position": v(-585, -170) * mm});
            skPoint(sketch, "E190", {"position": v(-410, -264.82) * mm});
            skPoint(sketch, "E191", {"position": v(-550, -264.82) * mm});
            skPoint(sketch, "E192", {"position": v(-410, -6.78) * mm});
            skPoint(sketch, "E193", {"position": v(-550, -6.78) * mm});
            skPoint(sketch, "E194", {"position": v(-410, 166.83) * mm});
            skPoint(sketch, "E195", {"position": v(-550, 166.83) * mm});
            skSolve(sketch);
        }
        {
            var Q0;
            Q0=sQuery(id+"F15.wireOp",VERTEX,"E186");
            var Q1;
            Q1=sQuery(id+"F15.wireOp",VERTEX,"E187");
            var Q2;
            Q2=sQuery(id+"F15.wireOp",VERTEX,"E195");
            var Q3;
            Q3=sQuery(id+"F15.wireOp",VERTEX,"E188");
            var Q4;
            Q4=sQuery(id+"F15.wireOp",VERTEX,"E193");
            var Q5;
            Q5=sQuery(id+"F15.wireOp",VERTEX,"E189");
            var Q6;
            Q6=sQuery(id+"F15.wireOp",VERTEX,"E191");
            var Q7;
            Q7=sQuery(id+"F15.wireOp",VERTEX,"E180");
            var Q8;
            Q8=sQuery(id+"F15.wireOp",VERTEX,"E190");
            var Q9;
            Q9=sQuery(id+"F15.wireOp",VERTEX,"E181");
            var Q10;
            Q10=sQuery(id+"F15.wireOp",VERTEX,"E182");
            var Q11;
            Q11=sQuery(id+"F15.wireOp",VERTEX,"E183");
            var Q12;
            Q12=sQuery(id+"F15.wireOp",VERTEX,"E192");
            var Q13;
            Q13=sQuery(id+"F15.wireOp",VERTEX,"E194");
            var Q14;
            Q14=sQuery(id+"F15.wireOp",VERTEX,"E184");
            var Q15;
            Q15=sQuery(id+"F15.wireOp",VERTEX,"E185");
            var Q16;
            Q16=makeQuery(id+"F4.opExtrude","SWEPT_BODY",BODY,{"disambiguationData":[OSD([sQuery(id+"F3.wireOp",EDGE,"E103.bottom"),sQuery(id+"F3.wireOp",EDGE,"E103.top"),sQuery(id+"F3.wireOp",EDGE,"E103.left"),sQuery(id+"F3.wireOp",EDGE,"E103.right")])]});
            hole(context, id + "F16", {"style" : HoleStyle.C_SINK, "endStyle" : HoleEndStyle.THROUGH, "standardTappedOrClearance" : lookupTablePath({ "fit" : "Normal", "standard" : "ISO", "size" : "M5", "type" : "Clearance" }), "standardBlindInLast" : lookupTablePath({ "fit" : "Normal", "standard" : "ISO", "engagement" : "75%", "pitch" : "0.8 mm", "size" : "M5", "type" : "Clearance & tapped" }), "holeDiameter" : 5.5 * mm, "cSinkDiameter" : 11.2 * mm, "cSinkAngle" : 90 * degree, "majorDiameter" : 5 * mm, "isTappedThrough" : true, "tappedDepth" : 12 * mm, "tapClearance" : 3, "locations" : qUnion([Q0, Q1, Q2, Q3, Q4, Q5, Q6, Q7, Q8, Q9, Q10, Q11, Q12, Q13, Q14, Q15]), "scope" : qUnion([Q16])});
        }
        {
            var Q0;
            Q0=makeQuery(id+"F4.opExtrude","CAP_FACE",FACE,{"disambiguationData":[OSD([sQuery(id+"F3.wireOp",EDGE,"E104.bottom"),sQuery(id+"F3.wireOp",EDGE,"E104.top"),sQuery(id+"F3.wireOp",EDGE,"E104.left"),sQuery(id+"F3.wireOp",EDGE,"E104.right"),sQuery(id+"F3.wireOp",EDGE,"E111.bottom"),sQuery(id+"F3.wireOp",EDGE,"E111.top"),sQuery(id+"F3.wireOp",EDGE,"E111.left"),sQuery(id+"F3.wireOp",EDGE,"E111.right")])],"isStart":false});
            var sketch = newSketch(context, id + "F17", { "sketchPlane" : qUnion([Q0])});
            skPoint(sketch, "E196", {"position": v(-1060, 93) * mm});
            skPoint(sketch, "E197", {"position": v(-975, 93) * mm});
            skPoint(sketch, "E198", {"position": v(-885, 93) * mm});
            skPoint(sketch, "E199", {"position": v(-800, 93) * mm});
            skPoint(sketch, "E200", {"position": v(-1060, 391) * mm});
            skPoint(sketch, "E201", {"position": v(-975, 391) * mm});
            skPoint(sketch, "E202", {"position": v(-885, 391) * mm});
            skPoint(sketch, "E203", {"position": v(-800, 391) * mm});
            skSolve(sketch);
        }
        {
            var Q0;
            Q0=sQuery(id+"F17.wireOp",VERTEX,"E199");
            var Q1;
            Q1=sQuery(id+"F17.wireOp",VERTEX,"E201");
            var Q2;
            Q2=sQuery(id+"F17.wireOp",VERTEX,"E203");
            var Q3;
            Q3=sQuery(id+"F17.wireOp",VERTEX,"E196");
            var Q4;
            Q4=sQuery(id+"F17.wireOp",VERTEX,"E200");
            var Q5;
            Q5=sQuery(id+"F17.wireOp",VERTEX,"E202");
            var Q6;
            Q6=sQuery(id+"F17.wireOp",VERTEX,"E197");
            var Q7;
            Q7=sQuery(id+"F17.wireOp",VERTEX,"E198");
            var Q8;
            Q8=makeQuery(id+"F4.opExtrude","SWEPT_BODY",BODY,{"disambiguationData":[OSD([sQuery(id+"F3.wireOp",EDGE,"E104.bottom"),sQuery(id+"F3.wireOp",EDGE,"E104.top"),sQuery(id+"F3.wireOp",EDGE,"E104.left"),sQuery(id+"F3.wireOp",EDGE,"E104.right"),sQuery(id+"F3.wireOp",EDGE,"E111.bottom"),sQuery(id+"F3.wireOp",EDGE,"E111.top"),sQuery(id+"F3.wireOp",EDGE,"E111.left"),sQuery(id+"F3.wireOp",EDGE,"E111.right")])]});
            hole(context, id + "F18", {"style" : HoleStyle.C_SINK, "endStyle" : HoleEndStyle.THROUGH, "standardTappedOrClearance" : lookupTablePath({ "fit" : "Normal", "standard" : "ISO", "size" : "M5", "type" : "Clearance" }), "standardBlindInLast" : lookupTablePath({ "fit" : "Normal", "standard" : "ISO", "engagement" : "75%", "pitch" : "0.8 mm", "size" : "M5", "type" : "Clearance & tapped" }), "holeDiameter" : 5.5 * mm, "cSinkDiameter" : 11.2 * mm, "cSinkAngle" : 90 * degree, "majorDiameter" : 5 * mm, "isTappedThrough" : true, "tappedDepth" : 12 * mm, "tapClearance" : 3, "locations" : qUnion([Q0, Q1, Q2, Q3, Q4, Q5, Q6, Q7]), "scope" : qUnion([Q8])});
        }
    });
